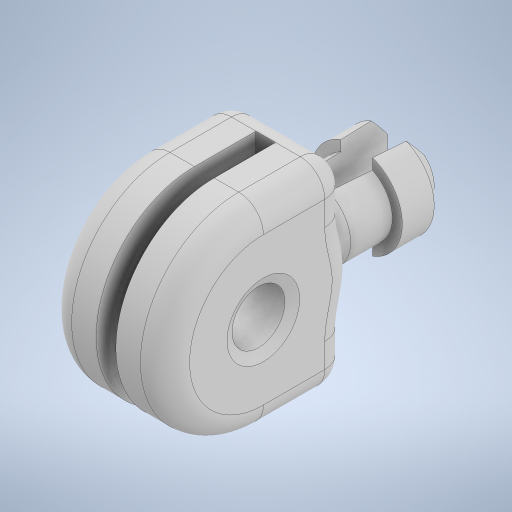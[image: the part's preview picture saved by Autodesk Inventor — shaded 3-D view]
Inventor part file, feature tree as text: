
AUTODESK INVENTOR PART (.ipt)
format: ipt  version: 2023.1 (Build 271208000, 208)  size: 400,384 bytes
history: native  units: mm
features: other x7, extrude x5, projected_geometry x3, chamfer x2, plane x1, loft x1, fillet x1
ambient origin geometry x8: Origin, YZ Plane, XZ Plane, XY Plane, X Axis, Y Axis, Z Axis, Center Point
bodies: Solid1 (feature_tree)
feature tree (20):
  extrude  "Clip Base"  Depth=8.0mm
  plane  "Work Plane (Slot Cut)"
  extrude  "Fin Slot Cut"  Depth=3.5mm
  extrude  "Snap Shaft"  Depth=2.15mm
  extrude  "Snap Lip"  Depth=4.8mm TaperAngle=0.0deg
  loft  "Snap Flex Cut"
  chamfer  "Entry Chamfer (Snap Tip)"  Distance=6.5mm
  fillet  "Body Fillets (Clip Base)"  Radius=2.9mm
  extrude  "Hex Nut Slot"  Depth=4.7mm TaperAngle=0.0deg
  chamfer  "Screw Head Chamfer (Outer Face)"  Distance=3.7mm
  other  "Base Profile"
  other  "Fin Slot Layout"
  other  "Shaft Profile"
  projected_geometry  "Projected Loop1"
  other  "Lip Profile"
  projected_geometry  "Projected Loop2"
  other  "Upper Flex Profile"
  projected_geometry  "Projected Loop3"
  other  "Lower Flex Profile"
  other  "Hex Slot Profile"
